# Revit family: BVN_BRDV
name_source: partatom
category: Mechanical Equipment
units: mm (PartAtom-declared; Revit-internal decimal feet)

## family parameters
Cut with Voids When Loaded = No
Host = Face
Part Type = Normal
Room Calculation Point = No
Round Connector Dimension = Use Diameter
Shared = No

## types (12) — shared parameters
Default Elevation = 1219 mm
Description = Roof Fan
Frequency = 50 Hz
I = 35 mm  [stored 0.114829 ft]
Insulation Class = F
Manufacturer = Bahçıvan Elektrik Motor San. ve Tic. Ltd. Şti.
Material = <By Category>
Model = BRDV
Protection Class = 55
URL = http://www.bahcivanmotor.com.tr
X = 250 mm  [stored 0.82021 ft]
int_ust = 250 mm  [stored 0.82021 ft]
t = 13 mm

## per-type parameters (varying)
| type | A | Air Flow | B | Capacitor (mF) | Current | D | D' | E | EF | F | G | Power | QC | QH | Sound Pressure Level dB(A) | Speed(d/d) | Voltage | Weight | h_Alt | h_Ust | int_L |
| BRDV 315M | 845 mm | 1900.0 m³/h | 740 mm | 10 | 2 A | 700 mm | 600 mm | 550 mm | 334 mm  [stored 1.0958 ft] | 395 mm  [stored 1.29593 ft] | 670 mm | 250 W | 185 mm  [stored 0.606955 ft] | 10 mm  [stored 0.0328084 ft] | 48 | 1380 | 230 V | 22.00 kg | 216 mm  [stored 0.708661 ft] | 144 mm  [stored 0.472441 ft] | 480 mm  [stored 1.5748 ft] |
| BRDV 355M | 845 mm | 2850.0 m³/h | 740 mm | 10 | 2 A | 700 mm | 600 mm | 550 mm | 334 mm  [stored 1.0958 ft] | 395 mm  [stored 1.29593 ft] | 670 mm | 250 W | 235 mm  [stored 0.770997 ft] | 10 mm  [stored 0.0328084 ft] | 50 | 1380 | 230 V | 27.00 kg | 216 mm  [stored 0.708661 ft] | 144 mm  [stored 0.472441 ft] | 500 mm  [stored 1.64042 ft] |
| BRDV 400M | 895 mm | 4000.0 m³/h | 780 mm | 15 | 3 A | 750 mm | 650 mm  [stored 2.13255 ft] | 585 mm  [stored 1.91929 ft] | 348 mm  [stored 1.14173 ft] | 430 mm | 720 mm | 370 W | 270 mm  [stored 0.885827 ft] | 10 mm  [stored 0.0328084 ft] | 51 | 1390 | 230 V | 33.00 kg | 237 mm  [stored 0.777559 ft] | 158 mm | 525 mm |
| BRDV 450M | 960 mm | 5300.0 m³/h | 855 mm | 20 | 5 A | 800 mm | 700 mm | 595 mm  [stored 1.9521 ft] | 352 mm | 440 mm  [stored 1.44357 ft] | 770 mm | 550 W | 282 mm | 10 mm  [stored 0.0328084 ft] | 54 | 1365 | 230 V | 38.00 kg | 243 mm  [stored 0.797244 ft] | 162 mm  [stored 0.531496 ft] | 550 mm |
| BRDV 500M | 1030 mm | 8000.0 m³/h | 915 mm | 35 | 8 A | 850 mm | 750 mm | 695 mm | 422 mm  [stored 1.38451 ft] | 490 mm  [stored 1.60761 ft] | 820 mm | 1100 W | 320 mm  [stored 1.04987 ft] | 14 mm  [stored 0.0459318 ft] | 56 | 1410 | 230 V | 49.00 kg | 273 mm  [stored 0.895669 ft] | 182 mm  [stored 0.597113 ft] | 600 mm |
| BRDV 560M | 1195 mm | 10500.0 m³/h | 960 mm | 50 | 14 A | 950 mm | 850 mm | 820 mm | 475 mm | 610 mm  [stored 2.00131 ft] | 920 mm | 2200 W | 360 mm  [stored 1.1811 ft] | 14 mm  [stored 0.0459318 ft] | 65 | 1420 | 230 V | 58.00 kg | 345 mm  [stored 1.13189 ft] | 230 mm  [stored 0.754593 ft] | 700 mm |
| BRDV 315T | 845 mm | 1900.0 m³/h | 740 mm | 0 | 1 A | 700 mm | 600 mm | 550 mm | 334 mm  [stored 1.0958 ft] | 395 mm  [stored 1.29593 ft] | 670 mm | 250 W | 185 mm  [stored 0.606955 ft] | 10 mm  [stored 0.0328084 ft] | 48 | 1380 | 380 V | 22.00 kg | 216 mm  [stored 0.708661 ft] | 144 mm  [stored 0.472441 ft] | 480 mm  [stored 1.5748 ft] |
| BRDV 355T | 845 mm | 2850.0 m³/h | 740 mm | 0 | 1 A | 700 mm | 600 mm | 550 mm | 334 mm  [stored 1.0958 ft] | 395 mm  [stored 1.29593 ft] | 670 mm | 250 W | 235 mm  [stored 0.770997 ft] | 10 mm  [stored 0.0328084 ft] | 50 | 1380 | 380 V | 27.00 kg | 216 mm  [stored 0.708661 ft] | 144 mm  [stored 0.472441 ft] | 500 mm  [stored 1.64042 ft] |
| BRDV 400T | 895 mm | 4000.0 m³/h | 780 mm | 0 | 1 A | 750 mm | 650 mm  [stored 2.13255 ft] | 585 mm  [stored 1.91929 ft] | 348 mm  [stored 1.14173 ft] | 430 mm | 720 mm | 370 W | 270 mm  [stored 0.885827 ft] | 10 mm  [stored 0.0328084 ft] | 51 | 1390 | 380 V | 33.00 kg | 237 mm  [stored 0.777559 ft] | 158 mm | 525 mm |
| BRDV 450T | 960 mm | 5300.0 m³/h | 855 mm | 0 | 2 A | 800 mm | 700 mm | 595 mm  [stored 1.9521 ft] | 352 mm | 440 mm  [stored 1.44357 ft] | 770 mm | 550 W | 282 mm | 10 mm  [stored 0.0328084 ft] | 54 | 1365 | 380 V | 38.00 kg | 243 mm  [stored 0.797244 ft] | 162 mm  [stored 0.531496 ft] | 550 mm |
| BRDV 500T | 1030 mm | 8000.0 m³/h | 915 mm | 0 | 3 A | 850 mm | 750 mm | 695 mm | 422 mm  [stored 1.38451 ft] | 490 mm  [stored 1.60761 ft] | 820 mm | 1100 W | 320 mm  [stored 1.04987 ft] | 14 mm  [stored 0.0459318 ft] | 56 | 1410 | 380 V | 49.00 kg | 273 mm  [stored 0.895669 ft] | 182 mm  [stored 0.597113 ft] | 600 mm |
| BRDV 560T | 1195 mm | 10500.0 m³/h | 960 mm | 0 | 5 A | 950 mm | 850 mm | 820 mm | 475 mm | 610 mm  [stored 2.00131 ft] | 920 mm | 2200 W | 360 mm  [stored 1.1811 ft] | 14 mm  [stored 0.0459318 ft] | 65 | 1420 | 380 V | 58.00 kg | 345 mm  [stored 1.13189 ft] | 230 mm  [stored 0.754593 ft] | 700 mm |

note: [stored X ft] marks values corroborated as IEEE doubles in the binary element streams (Revit-internal decimal feet)

## geometry (parser evidence)
native form markers: Sweep x2
no freeform markers — native parametric forms only
